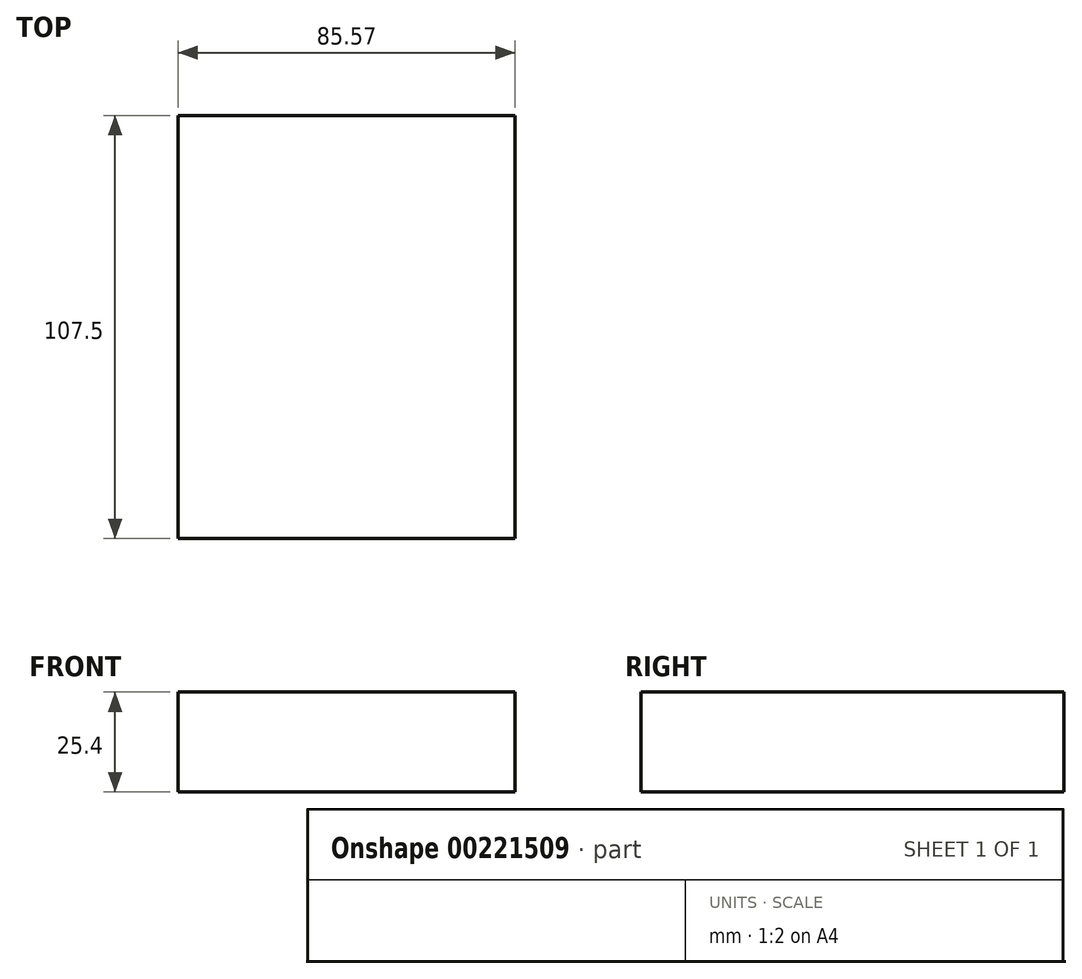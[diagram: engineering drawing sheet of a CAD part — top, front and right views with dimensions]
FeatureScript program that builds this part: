
annotation { "Feature Type Name" : "Feature", "Feature Type Description" : "" }
export const myFeature = defineFeature(function(context is Context, id is Id, definition is map)
    precondition{}
    {
        {
            var Q0;
            Q0=qCreatedBy(makeId("Top.planeOp"),FACE);
            var sketch = newSketch(context, id + "F0", { "sketchPlane" : qUnion([Q0])});
            skLineSegment(sketch, "E0.bottom", {"start": v(0, 0) * mm, "end": v(85.57, 0) * mm});
            skLineSegment(sketch, "E0.top", {"start": v(0, 107.5) * mm, "end": v(85.57, 107.5) * mm});
            skLineSegment(sketch, "E0.left", {"start": v(0, 0) * mm, "end": v(0, 107.5) * mm});
            skLineSegment(sketch, "E0.right", {"start": v(85.57, 0) * mm, "end": v(85.57, 107.5) * mm});
            skSolve(sketch);
        }
        {
            var Q0;
            Q0 = qSketchRegion(id + "F0", true);
            extrude(context, id + "F1", {"entities" : qUnion([Q0]), "depth" : 25.4 * mm});
        }
    });
